# Revit family: DuctPanel_Curtainwall_ASI-Alpaco_Frameless
name_source: partatom
category: Curtain Panels
revit_build: Autodesk Revit 2015 (Build: 20140606_1530(x64)
units: mm (PartAtom-declared; Revit-internal decimal feet)

## types (2) — shared parameters
Assembly Code = C3010140
Cover Panel Finish = CoverPanel_ExampleFinish
Cover Panel Thickness = 0' - 0 1/2"
Description = ASI Alpaco Panel
Flash Panel Finish = <By Category>
Flash Panel Thickness = 0' - 0 1/2"
Flash Panel Width = 0' - 5 1/8"
Frame Depth = 0' - 1 9/16"
Frame Finish = <By Category>
Frame Reveal = 0' - 3 15/16"
Frame Width = 0' - 1 3/16"
Keynote = 06 26 00
Manufacturer = ASI-Alpaco
Model = Alpaco
URL = http://americanspecialties.com
zero-valued in all types: Cost

## per-type parameters (varying)
| type | Panel Type |
| Fixed Panel | DuctPanel_ASI-Alpaco_Frameless : Fixed Panel |
| Access Panel | DuctPanel_ASI-Alpaco_Frameless : Access Panel |

## geometry (parser evidence)
native form markers: Sweep x5
no freeform markers — native parametric forms only
